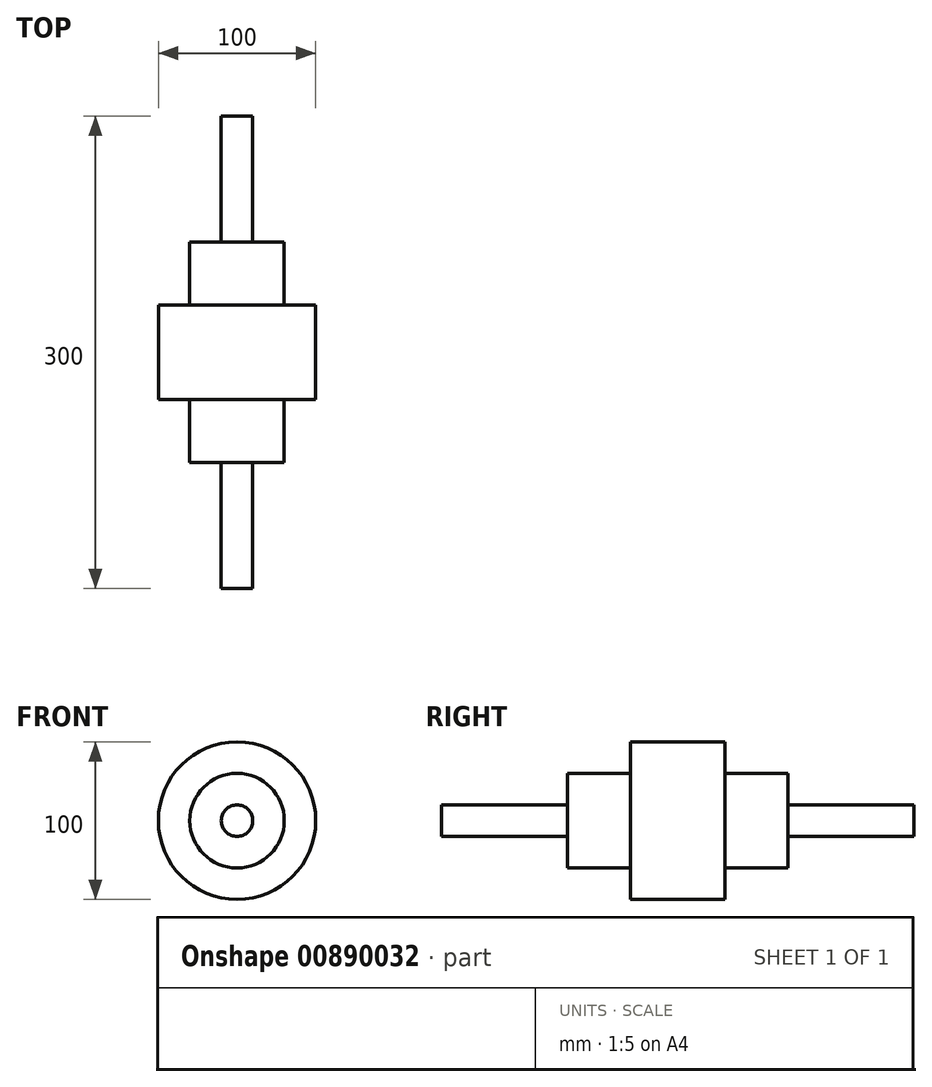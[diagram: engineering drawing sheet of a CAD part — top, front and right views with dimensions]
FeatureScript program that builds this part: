
annotation { "Feature Type Name" : "Feature", "Feature Type Description" : "" }
export const myFeature = defineFeature(function(context is Context, id is Id, definition is map)
    precondition{}
    {
        {
            var Q0;
            Q0=qCreatedBy(makeId("Front.planeOp"),FACE);
            var sketch = newSketch(context, id + "F0", { "sketchPlane" : qUnion([Q0])});
            skCircle(sketch, "E0", {"center": v(0, 0) * mm, "radius": 50 * mm});
            skSolve(sketch);
        }
        {
            var Q0;
            Q0=makeQuery(id+"F0.imprint","IMPRINT",FACE,{"disambiguationData":[TD([[makeQuery(id+"F0.imprint","IMPRINT",EDGE,{"derivedFrom":sQuery(id+"F0.wireOp",EDGE,"E0")}),1.0]])]});
            extrude(context, id + "F1", {"entities" : qUnion([Q0]), "depth" : 30 * mm, "offsetDistance" : 25.4 * mm});
        }
        {
            var Q0;
            Q0=makeQuery(id+"F1.opExtrude","CAP_FACE",FACE,{"disambiguationData":[OSD([sQuery(id+"F0.wireOp",EDGE,"E0")])],"isStart":true});
            extrude(context, id + "F2", {"entities" : qUnion([Q0]), "operationType" : NewBodyOperationType.ADD, "depth" : 30 * mm, "offsetDistance" : 25.4 * mm});
        }
        {
            var Q0;
            Q0=makeQuery(id+"F1.opExtrude","CAP_FACE",FACE,{"disambiguationData":[OSD([sQuery(id+"F0.wireOp",EDGE,"E0")])],"isStart":false});
            var sketch = newSketch(context, id + "F3", { "sketchPlane" : qUnion([Q0])});
            skCircle(sketch, "E1", {"center": v(0, 0) * mm, "radius": 30 * mm});
            skSolve(sketch);
        }
        {
            var Q0;
            Q0 = qSketchRegion(id + "F3", true);
            extrude(context, id + "F4", {"entities" : qUnion([Q0]), "operationType" : NewBodyOperationType.ADD, "depth" : 40 * mm, "offsetDistance" : 25.4 * mm});
        }
        {
            var Q0;
            Q0=makeQuery(id+"F2.opExtrude","CAP_FACE",FACE,{"disambiguationData":[OSD([sQuery(id+"F0.wireOp",EDGE,"E0")])],"isStart":false});
            var sketch = newSketch(context, id + "F5", { "sketchPlane" : qUnion([Q0])});
            skCircle(sketch, "E2", {"center": v(0, 0) * mm, "radius": 30 * mm});
            skSolve(sketch);
        }
        {
            var Q0;
            Q0 = qSketchRegion(id + "F5", true);
            extrude(context, id + "F6", {"entities" : qUnion([Q0]), "operationType" : NewBodyOperationType.ADD, "depth" : 40 * mm, "offsetDistance" : 25.4 * mm});
        }
        {
            var Q0;
            Q0=makeQuery(id+"F4.opExtrude","CAP_FACE",FACE,{"disambiguationData":[OSD([sQuery(id+"F3.wireOp",EDGE,"E1")])],"isStart":false});
            var sketch = newSketch(context, id + "F7", { "sketchPlane" : qUnion([Q0])});
            skCircle(sketch, "E3", {"center": v(0, 0) * mm, "radius": 10 * mm});
            skSolve(sketch);
        }
        {
            var Q0;
            Q0 = qSketchRegion(id + "F7", true);
            extrude(context, id + "F8", {"entities" : qUnion([Q0]), "operationType" : NewBodyOperationType.ADD, "depth" : 80 * mm, "offsetDistance" : 25.4 * mm});
        }
        {
            var Q0;
            Q0=makeQuery(id+"F6.opExtrude","CAP_FACE",FACE,{"disambiguationData":[OSD([sQuery(id+"F5.wireOp",EDGE,"E2")])],"isStart":false});
            var sketch = newSketch(context, id + "F9", { "sketchPlane" : qUnion([Q0])});
            skCircle(sketch, "E4", {"center": v(0, 0) * mm, "radius": 10 * mm});
            skSolve(sketch);
        }
        {
            var Q0;
            Q0=makeQuery(id+"F9.imprint","IMPRINT",FACE,{"disambiguationData":[TD([[makeQuery(id+"F9.imprint","IMPRINT",EDGE,{"derivedFrom":sQuery(id+"F9.wireOp",EDGE,"E4")}),1.0]])]});
            extrude(context, id + "F10", {"entities" : qUnion([Q0]), "operationType" : NewBodyOperationType.ADD, "depth" : 80 * mm, "offsetDistance" : 25.4 * mm});
        }
    });
